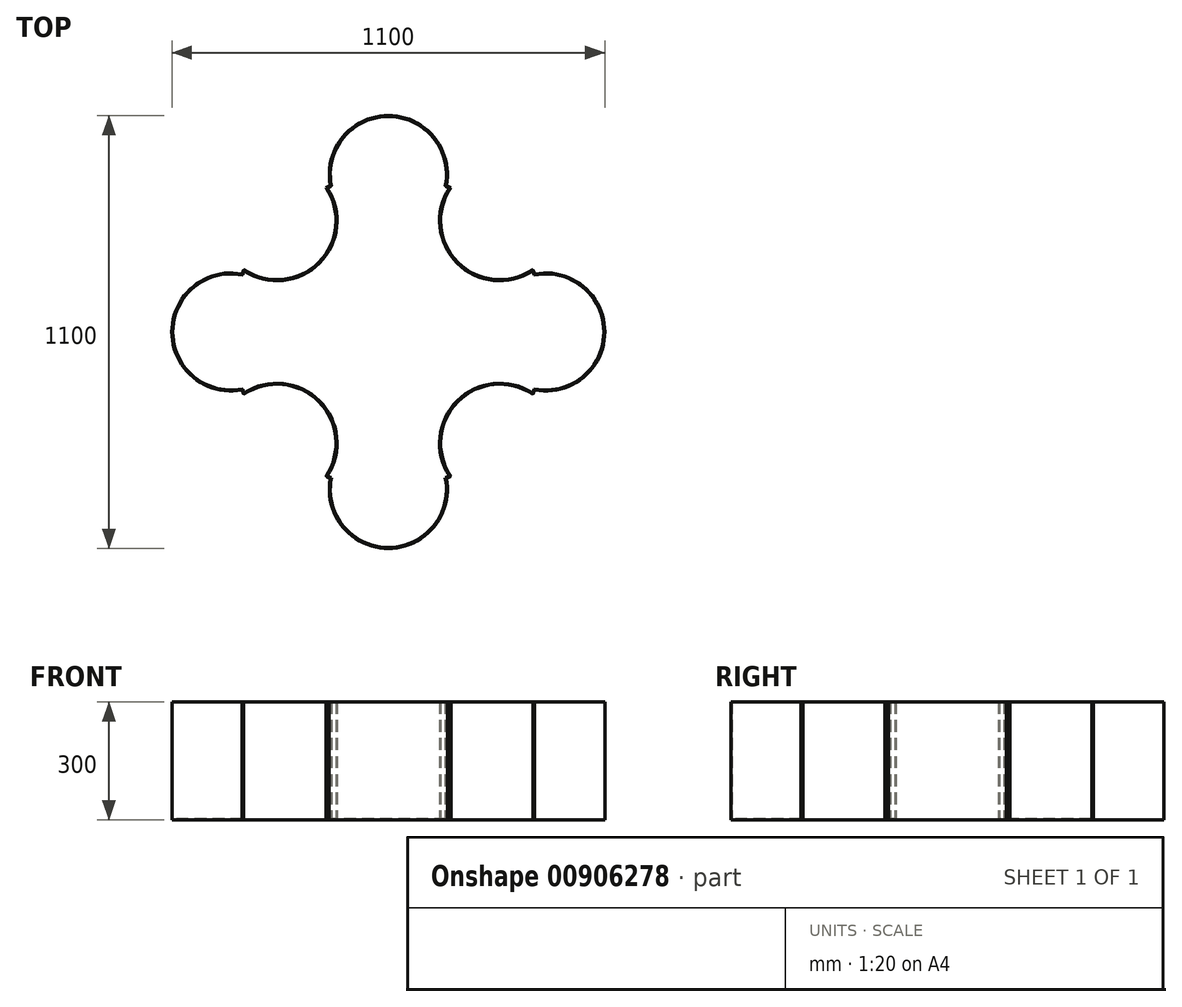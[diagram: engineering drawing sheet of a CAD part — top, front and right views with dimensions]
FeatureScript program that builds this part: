
annotation { "Feature Type Name" : "Feature", "Feature Type Description" : "" }
export const myFeature = defineFeature(function(context is Context, id is Id, definition is map)
    precondition{}
    {
        {
            var Q0;
            Q0=qCreatedBy(makeId("Top.planeOp"),FACE);
            var sketch = newSketch(context, id + "F0", { "sketchPlane" : qUnion([Q0])});
            skArc(sketch, "E0", {"start": v(-367.14, 158.77) * mm, "mid": v(-369.55, 153.07) * mm, "end": v(-371.88, 147.34) * mm});
            skArc(sketch, "E1", {"start": v(147.34, 371.87) * mm, "mid": v(0, 550) * mm, "end": v(-147.34, 371.88) * mm});
            skArc(sketch, "E2", {"start": v(-367.14, 158.77) * mm, "mid": v(-176.78, 176.78) * mm, "end": v(-158.77, 367.14) * mm});
            skArc(sketch, "E3", {"start": v(-371.88, 147.34) * mm, "mid": v(-550, 0) * mm, "end": v(-371.88, -147.34) * mm});
            skArc(sketch, "E4", {"start": v(-158.77, -367.14) * mm, "mid": v(-176.78, -176.78) * mm, "end": v(-367.14, -158.77) * mm});
            skArc(sketch, "E5", {"start": v(-147.34, -371.88) * mm, "mid": v(0, -550) * mm, "end": v(147.34, -371.87) * mm});
            skArc(sketch, "E6", {"start": v(367.14, -158.77) * mm, "mid": v(176.78, -176.78) * mm, "end": v(158.77, -367.14) * mm});
            skArc(sketch, "E7", {"start": v(371.87, -147.34) * mm, "mid": v(550, 0) * mm, "end": v(371.88, 147.34) * mm});
            skArc(sketch, "E8", {"start": v(158.77, 367.14) * mm, "mid": v(176.78, 176.78) * mm, "end": v(367.14, 158.77) * mm});
            skArc(sketch, "E9.trimOffspring", {"start": v(-147.34, 371.88) * mm, "mid": v(-153.07, 369.55) * mm, "end": v(-158.77, 367.14) * mm});
            skArc(sketch, "E10.trimOffspring", {"start": v(158.77, 367.14) * mm, "mid": v(153.07, 369.55) * mm, "end": v(147.34, 371.87) * mm});
            skArc(sketch, "E11.trimOffspring", {"start": v(-158.77, -367.14) * mm, "mid": v(-153.07, -369.55) * mm, "end": v(-147.34, -371.88) * mm});
            skArc(sketch, "E12.trimOffspring", {"start": v(367.14, -158.77) * mm, "mid": v(369.55, -153.07) * mm, "end": v(371.88, -147.34) * mm});
            skArc(sketch, "E13.trimOffspring", {"start": v(147.34, -371.87) * mm, "mid": v(153.07, -369.55) * mm, "end": v(158.77, -367.14) * mm});
            skArc(sketch, "E14.trimOffspring", {"start": v(371.88, 147.34) * mm, "mid": v(369.55, 153.07) * mm, "end": v(367.14, 158.77) * mm});
            skArc(sketch, "E15.trimOffspring", {"start": v(-371.88, -147.34) * mm, "mid": v(-369.55, -153.07) * mm, "end": v(-367.14, -158.77) * mm});
            skSolve(sketch);
        }
        {
            var Q0;
            Q0=makeQuery(id+"F0.imprint","IMPRINT",FACE,{"disambiguationData":[TD([[makeQuery(id+"F0.imprint","IMPRINT",EDGE,{"derivedFrom":sQuery(id+"F0.wireOp",EDGE,"E0")}),1.0]])]});
            extrude(context, id + "F1", {"entities" : qUnion([Q0]), "depth" : 300 * mm, "offsetDistance" : 25 * mm});
        }
        {
            var Q0;
            Q0=makeQuery(id+"F1.opExtrude","CAP_FACE",FACE,{"disambiguationData":[OSD([sQuery(id+"F0.wireOp",EDGE,"E0"),sQuery(id+"F0.wireOp",EDGE,"E1"),sQuery(id+"F0.wireOp",EDGE,"E2"),sQuery(id+"F0.wireOp",EDGE,"E3"),sQuery(id+"F0.wireOp",EDGE,"E4"),sQuery(id+"F0.wireOp",EDGE,"E5"),sQuery(id+"F0.wireOp",EDGE,"E6"),sQuery(id+"F0.wireOp",EDGE,"E7"),sQuery(id+"F0.wireOp",EDGE,"E8"),sQuery(id+"F0.wireOp",EDGE,"E9.trimOffspring"),sQuery(id+"F0.wireOp",EDGE,"E10.trimOffspring"),sQuery(id+"F0.wireOp",EDGE,"E11.trimOffspring"),sQuery(id+"F0.wireOp",EDGE,"E12.trimOffspring"),sQuery(id+"F0.wireOp",EDGE,"E13.trimOffspring"),sQuery(id+"F0.wireOp",EDGE,"E14.trimOffspring"),sQuery(id+"F0.wireOp",EDGE,"E15.trimOffspring")])],"isStart":false});
            shell(context, id + "F2", {"entities" : qUnion([Q0]), "thickness" : 2.5 * mm});
        }
    });
